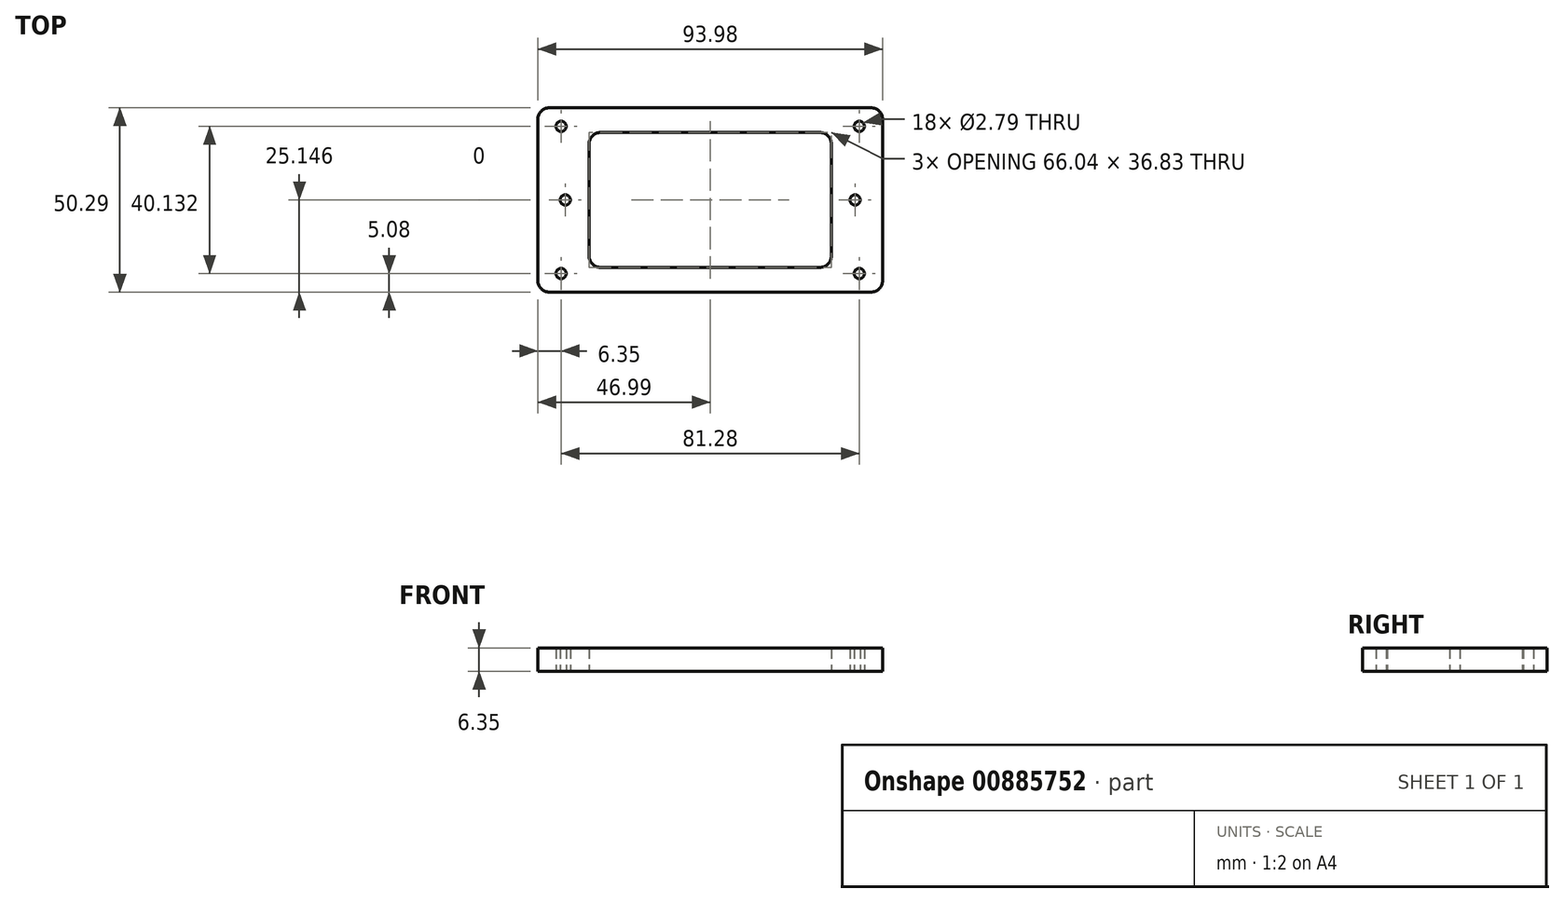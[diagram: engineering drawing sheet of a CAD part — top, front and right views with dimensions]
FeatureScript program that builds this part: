
annotation { "Feature Type Name" : "Feature", "Feature Type Description" : "" }
export const myFeature = defineFeature(function(context is Context, id is Id, definition is map)
    precondition{}
    {
        {
            var Q0;
            Q0=qCreatedBy(makeId("Top.planeOp"),FACE);
            var sketch = newSketch(context, id + "F0", { "sketchPlane" : qUnion([Q0])});
            skLineSegment(sketch, "E0.bottom", {"start": v(3.18, 0) * mm, "end": v(90.8, 0) * mm});
            skLineSegment(sketch, "E0.top", {"start": v(3.17, 50.3) * mm, "end": v(90.8, 50.3) * mm});
            skLineSegment(sketch, "E0.left", {"start": v(0, 3.18) * mm, "end": v(0, 47.12) * mm});
            skLineSegment(sketch, "E0.right", {"start": v(93.98, 3.18) * mm, "end": v(93.98, 47.12) * mm});
            skLineSegment(sketch, "E1.0", {"start": v(17.14, 6.73) * mm, "end": v(76.83, 6.73) * mm});
            skLineSegment(sketch, "E2.0", {"start": v(17.14, 43.56) * mm, "end": v(76.83, 43.56) * mm});
            skLineSegment(sketch, "E3.0", {"start": v(13.97, 9.9) * mm, "end": v(13.97, 40.39) * mm});
            skLineSegment(sketch, "E4.0", {"start": v(80, 9.9) * mm, "end": v(80, 40.39) * mm});
            skLineSegment(sketch, "E5", {"start": v(6.35, 50.3) * mm, "end": v(6.35, 0) * mm, "construction": true});
            skLineSegment(sketch, "E6", {"start": v(87.63, 50.3) * mm, "end": v(87.63, 0) * mm, "construction": true});
            skLineSegment(sketch, "E7", {"start": v(0, 45.21) * mm, "end": v(93.98, 45.21) * mm, "construction": true});
            skLineSegment(sketch, "E8", {"start": v(0, 5.08) * mm, "end": v(93.98, 5.08) * mm, "construction": true});
            skLineSegment(sketch, "E9", {"start": v(0, 25.15) * mm, "end": v(93.98, 25.15) * mm, "construction": true});
            skLineSegment(sketch, "E10", {"start": v(7.5, 50.3) * mm, "end": v(7.5, 0) * mm, "construction": true});
            skLineSegment(sketch, "E11", {"start": v(86.49, 50.3) * mm, "end": v(86.49, 0) * mm, "construction": true});
            skCircle(sketch, "E12", {"center": v(6.35, 45.21) * mm, "radius": 1.4 * mm});
            skCircle(sketch, "E13", {"center": v(7.5, 25.15) * mm, "radius": 1.4 * mm});
            skCircle(sketch, "E14", {"center": v(6.35, 5.08) * mm, "radius": 1.4 * mm});
            skCircle(sketch, "E15", {"center": v(87.63, 5.08) * mm, "radius": 1.4 * mm});
            skCircle(sketch, "E16", {"center": v(86.49, 25.15) * mm, "radius": 1.4 * mm});
            skCircle(sketch, "E17", {"center": v(87.63, 45.21) * mm, "radius": 1.4 * mm});
            skPoint(sketch, "E18.visualSharp", {"position": v(0, 50.3) * mm});
            skArc(sketch, "E18.filletArc", {"start": v(3.17, 50.3) * mm, "mid": v(0.93, 49.36) * mm, "end": v(0, 47.12) * mm});
            skPoint(sketch, "E19.visualSharp", {"position": v(0, 0) * mm});
            skArc(sketch, "E19.filletArc", {"start": v(0, 3.18) * mm, "mid": v(0.93, 0.93) * mm, "end": v(3.18, 0) * mm});
            skPoint(sketch, "E20.visualSharp", {"position": v(93.98, 0) * mm});
            skArc(sketch, "E20.filletArc", {"start": v(90.8, 0) * mm, "mid": v(93.05, 0.93) * mm, "end": v(93.98, 3.18) * mm});
            skPoint(sketch, "E21.visualSharp", {"position": v(93.98, 50.3) * mm});
            skArc(sketch, "E21.filletArc", {"start": v(93.98, 47.12) * mm, "mid": v(93.05, 49.36) * mm, "end": v(90.8, 50.3) * mm});
            skPoint(sketch, "E22.visualSharp", {"position": v(80, 43.56) * mm});
            skArc(sketch, "E22.filletArc", {"start": v(80, 40.39) * mm, "mid": v(79.08, 42.63) * mm, "end": v(76.83, 43.56) * mm});
            skPoint(sketch, "E23.visualSharp", {"position": v(80, 6.73) * mm});
            skArc(sketch, "E23.filletArc", {"start": v(76.83, 6.73) * mm, "mid": v(79.08, 7.66) * mm, "end": v(80, 9.9) * mm});
            skPoint(sketch, "E24.visualSharp", {"position": v(13.97, 6.73) * mm});
            skArc(sketch, "E24.filletArc", {"start": v(13.97, 9.9) * mm, "mid": v(14.9, 7.66) * mm, "end": v(17.14, 6.73) * mm});
            skPoint(sketch, "E25.visualSharp", {"position": v(13.97, 43.56) * mm});
            skArc(sketch, "E25.filletArc", {"start": v(17.14, 43.56) * mm, "mid": v(14.9, 42.63) * mm, "end": v(13.97, 40.39) * mm});
            skSolve(sketch);
        }
        {
            var Q0;
            Q0 = qSketchRegion(id + "F0", true);
            extrude(context, id + "F1", {"entities" : qUnion([Q0]), "depth" : 6.35 * mm, "offsetDistance" : 25.4 * mm});
        }
    });
